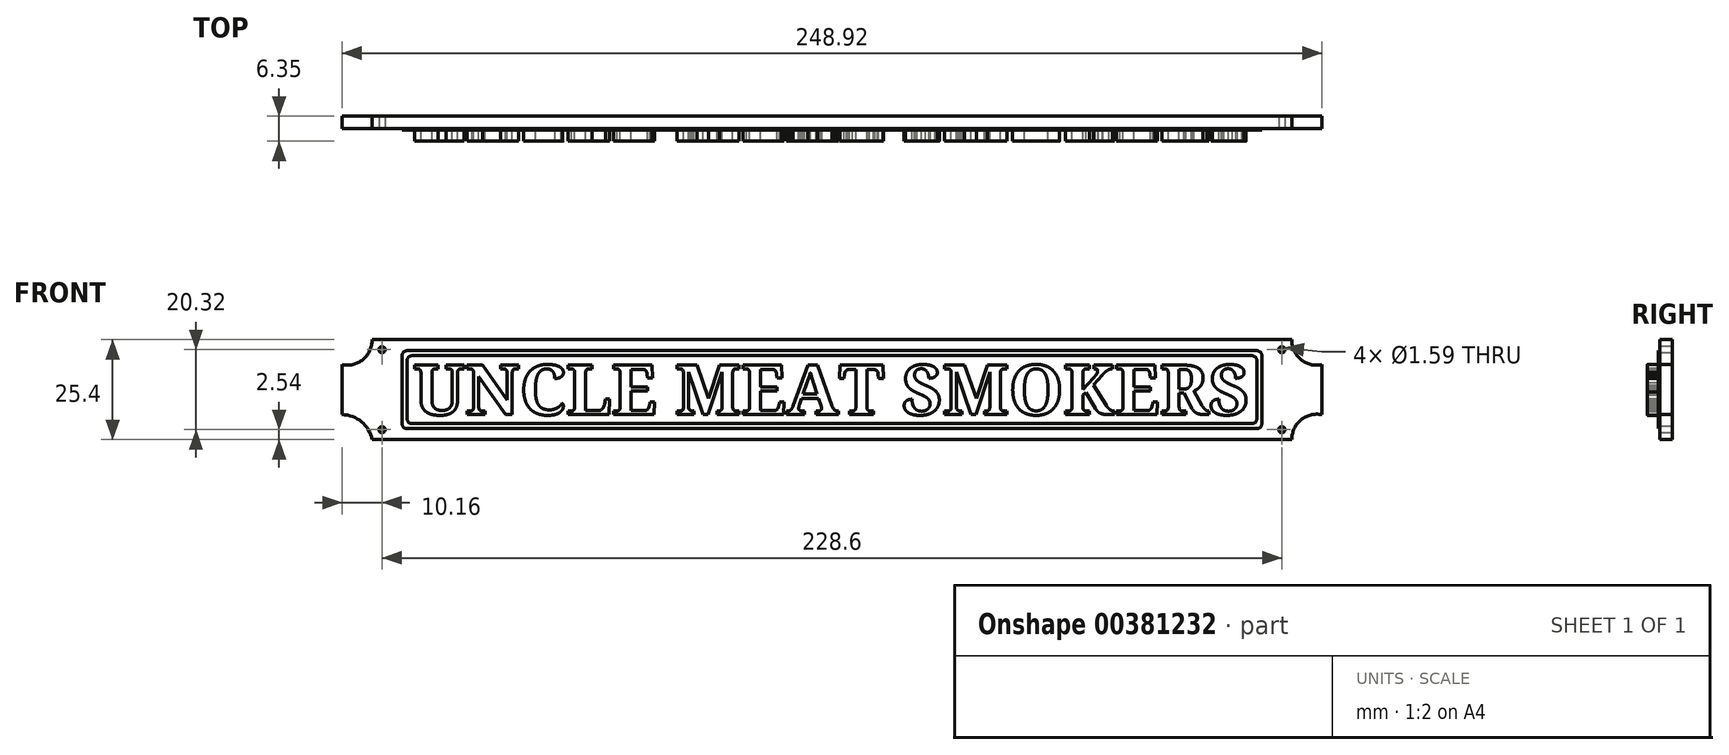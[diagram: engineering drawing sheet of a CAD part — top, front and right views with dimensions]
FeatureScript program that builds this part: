
annotation { "Feature Type Name" : "Feature", "Feature Type Description" : "" }
export const myFeature = defineFeature(function(context is Context, id is Id, definition is map)
    precondition{}
    {
        {
            var Q0;
            Q0=qCreatedBy(makeId("Front.planeOp"),FACE);
            var sketch = newSketch(context, id + "F0", { "sketchPlane" : qUnion([Q0])});
            skLineSegment(sketch, "E0.bottom", {"start": v(-116.84, 12.7) * mm, "end": v(116.84, 12.7) * mm});
            skLineSegment(sketch, "E0.top", {"start": v(-116.84, -12.7) * mm, "end": v(116.84, -12.7) * mm});
            skLineSegment(sketch, "E0.left", {"start": v(-124.46, 6.35) * mm, "end": v(-124.46, -6.35) * mm});
            skLineSegment(sketch, "E0.right", {"start": v(124.46, 6.35) * mm, "end": v(124.46, -6.35) * mm});
            skArc(sketch, "E1", {"start": v(-124.46, 6.35) * mm, "mid": v(-119.12, 7.7) * mm, "end": v(-116.84, 12.7) * mm});
            skArc(sketch, "E2", {"start": v(-116.84, -12.7) * mm, "mid": v(-119.5, -8.15) * mm, "end": v(-124.46, -6.35) * mm});
            skArc(sketch, "E3", {"start": v(124.46, -6.35) * mm, "mid": v(119.12, -7.7) * mm, "end": v(116.84, -12.7) * mm});
            skArc(sketch, "E4", {"start": v(116.84, 12.7) * mm, "mid": v(119.12, 7.7) * mm, "end": v(124.46, 6.35) * mm});
            skPoint(sketch, "E5.orphan", {"position": v(-124.46, -12.7) * mm});
            skSolve(sketch);
        }
        {
            var Q0;
            Q0 = qSketchRegion(id + "F0", true);
            extrude(context, id + "F1", {"entities" : qUnion([Q0]), "depth" : 3.17 * mm});
        }
        {
            var Q0;
            Q0=makeQuery(id+"F1.opExtrude","CAP_FACE",FACE,{"disambiguationData":[OSD([sQuery(id+"F0.wireOp",EDGE,"E0.bottom"),sQuery(id+"F0.wireOp",EDGE,"E0.top"),sQuery(id+"F0.wireOp",EDGE,"E0.left"),sQuery(id+"F0.wireOp",EDGE,"E0.right"),sQuery(id+"F0.wireOp",EDGE,"E1"),sQuery(id+"F0.wireOp",EDGE,"E2"),sQuery(id+"F0.wireOp",EDGE,"E3"),sQuery(id+"F0.wireOp",EDGE,"E4")])],"isStart":false});
            var sketch = newSketch(context, id + "F2", { "sketchPlane" : qUnion([Q0])});
            skLineSegment(sketch, "E6", {"start": v(-124.46, -6.35) * mm, "end": v(124.46, -6.35) * mm, "construction": true});
            skText(sketch, "E7", { "text": "UNCLE MEAT SMOKERS", "fontName": "NotoSerif-Bold.ttf"});
            const initialGuessF2  = {"E7": [-0.10636, -0.00635, 1, 0, 0.0127]};
            skSetInitialGuess(sketch, initialGuessF2);
            skSolve(sketch);
        }
        {
            var Q0;
            Q0 = qSketchRegion(id + "F2", true);
            extrude(context, id + "F3", {"entities" : qUnion([Q0]), "operationType" : NewBodyOperationType.ADD, "depth" : 3.17 * mm});
        }
        {
            var Q0;
            {var subQ0=sQuery(id+"F0.wireOp",EDGE,"E4");var subQ1=sQuery(id+"F0.wireOp",EDGE,"E3");var subQ2=sQuery(id+"F0.wireOp",EDGE,"E2");var subQ3=sQuery(id+"F0.wireOp",EDGE,"E1");var subQ4=sQuery(id+"F0.wireOp",EDGE,"E0.top");var subQ5=sQuery(id+"F0.wireOp",EDGE,"E0.right");var subQ6=sQuery(id+"F0.wireOp",EDGE,"E0.bottom");var subQ7=sQuery(id+"F0.wireOp",EDGE,"E0.left");Q0=makeQuery(id+"F3.boolean.opBoolean","SPLIT",FACE,{"disambiguationData":[TD([makeQuery(id+"F1.opExtrude","SWEPT_FACE",FACE,{"disambiguationData":[OSD([subQ6])]})])],"derivedFrom":makeQuery(id+"F1.opExtrude","CAP_FACE",FACE,{"disambiguationData":[OSD([subQ6,subQ4,subQ7,subQ5,subQ3,subQ2,subQ1,subQ0])],"isStart":false})});}
            var sketch = newSketch(context, id + "F4", { "sketchPlane" : qUnion([Q0])});
            skCircle(sketch, "E8", {"center": v(-114.3, 10.16) * mm, "radius": 0.8 * mm});
            skCircle(sketch, "E9", {"center": v(-114.3, -10.16) * mm, "radius": 0.8 * mm});
            skCircle(sketch, "E10", {"center": v(114.3, -10.16) * mm, "radius": 0.8 * mm});
            skCircle(sketch, "E11", {"center": v(114.3, 10.16) * mm, "radius": 0.8 * mm});
            skSolve(sketch);
        }
        {
            var Q0;
            Q0 = qSketchRegion(id + "F4", true);
            extrude(context, id + "F5", {"entities" : qUnion([Q0]), "operationType" : NewBodyOperationType.REMOVE, "oppositeDirection" : true, "depth" : 25.4 * mm});
        }
        {
            var Q0;
            {var subQ0=sQuery(id+"F0.wireOp",EDGE,"E4");var subQ1=sQuery(id+"F0.wireOp",EDGE,"E3");var subQ2=sQuery(id+"F0.wireOp",EDGE,"E2");var subQ3=sQuery(id+"F0.wireOp",EDGE,"E1");var subQ4=sQuery(id+"F0.wireOp",EDGE,"E0.top");var subQ5=sQuery(id+"F0.wireOp",EDGE,"E0.right");var subQ6=sQuery(id+"F0.wireOp",EDGE,"E0.bottom");var subQ7=sQuery(id+"F0.wireOp",EDGE,"E0.left");Q0=makeQuery(id+"F3.boolean.opBoolean","SPLIT",FACE,{"disambiguationData":[TD([makeQuery(id+"F1.opExtrude","SWEPT_FACE",FACE,{"disambiguationData":[OSD([subQ6])]})])],"derivedFrom":makeQuery(id+"F1.opExtrude","CAP_FACE",FACE,{"disambiguationData":[OSD([subQ6,subQ4,subQ7,subQ5,subQ3,subQ2,subQ1,subQ0])],"isStart":false})});}
            var sketch = newSketch(context, id + "F6", { "sketchPlane" : qUnion([Q0])});
            skLineSegment(sketch, "E12.bottom", {"start": v(-106.68, 8.64) * mm, "end": v(106.68, 8.64) * mm});
            skLineSegment(sketch, "E12.top", {"start": v(-106.68, -8.64) * mm, "end": v(106.68, -8.64) * mm});
            skLineSegment(sketch, "E12.left", {"start": v(-107.95, 7.37) * mm, "end": v(-107.95, -7.37) * mm});
            skLineSegment(sketch, "E12.right", {"start": v(107.95, 7.37) * mm, "end": v(107.95, -7.37) * mm});
            skLineSegment(sketch, "E13.bottom", {"start": v(-107.95, 9.9) * mm, "end": v(107.95, 9.9) * mm});
            skLineSegment(sketch, "E13.top", {"start": v(-107.95, -9.9) * mm, "end": v(107.95, -9.9) * mm});
            skLineSegment(sketch, "E13.left", {"start": v(-109.22, 8.64) * mm, "end": v(-109.22, -8.64) * mm});
            skLineSegment(sketch, "E13.right", {"start": v(109.22, 8.64) * mm, "end": v(109.22, -8.64) * mm});
            skPoint(sketch, "E14.visualSharp", {"position": v(-107.95, -8.64) * mm});
            skArc(sketch, "E14.filletArc", {"start": v(-107.95, -7.37) * mm, "mid": v(-107.58, -8.26) * mm, "end": v(-106.68, -8.64) * mm});
            skPoint(sketch, "E15.visualSharp", {"position": v(-107.95, 8.64) * mm});
            skArc(sketch, "E15.filletArc", {"start": v(-106.68, 8.64) * mm, "mid": v(-107.58, 8.26) * mm, "end": v(-107.95, 7.37) * mm});
            skPoint(sketch, "E16.visualSharp", {"position": v(107.95, 8.64) * mm});
            skArc(sketch, "E16.filletArc", {"start": v(107.95, 7.37) * mm, "mid": v(107.58, 8.26) * mm, "end": v(106.68, 8.64) * mm});
            skPoint(sketch, "E17.visualSharp", {"position": v(107.95, -8.64) * mm});
            skArc(sketch, "E17.filletArc", {"start": v(106.68, -8.64) * mm, "mid": v(107.58, -8.26) * mm, "end": v(107.95, -7.37) * mm});
            skPoint(sketch, "E18.visualSharp", {"position": v(109.22, -9.9) * mm});
            skArc(sketch, "E18.filletArc", {"start": v(107.95, -9.9) * mm, "mid": v(108.85, -9.53) * mm, "end": v(109.22, -8.64) * mm});
            skPoint(sketch, "E19.visualSharp", {"position": v(109.22, 9.9) * mm});
            skArc(sketch, "E19.filletArc", {"start": v(109.22, 8.64) * mm, "mid": v(108.85, 9.53) * mm, "end": v(107.95, 9.9) * mm});
            skPoint(sketch, "E20.visualSharp", {"position": v(-109.22, 9.9) * mm});
            skArc(sketch, "E20.filletArc", {"start": v(-107.95, 9.9) * mm, "mid": v(-108.85, 9.53) * mm, "end": v(-109.22, 8.64) * mm});
            skPoint(sketch, "E21.visualSharp", {"position": v(-109.22, -9.9) * mm});
            skArc(sketch, "E21.filletArc", {"start": v(-109.22, -8.64) * mm, "mid": v(-108.85, -9.53) * mm, "end": v(-107.95, -9.9) * mm});
            skSolve(sketch);
        }
        {
            var Q0;
            Q0 = qSketchRegion(id + "F6", true);
            extrude(context, id + "F7", {"entities" : qUnion([Q0]), "operationType" : NewBodyOperationType.ADD, "depth" : 0.4 * mm});
        }
    });
